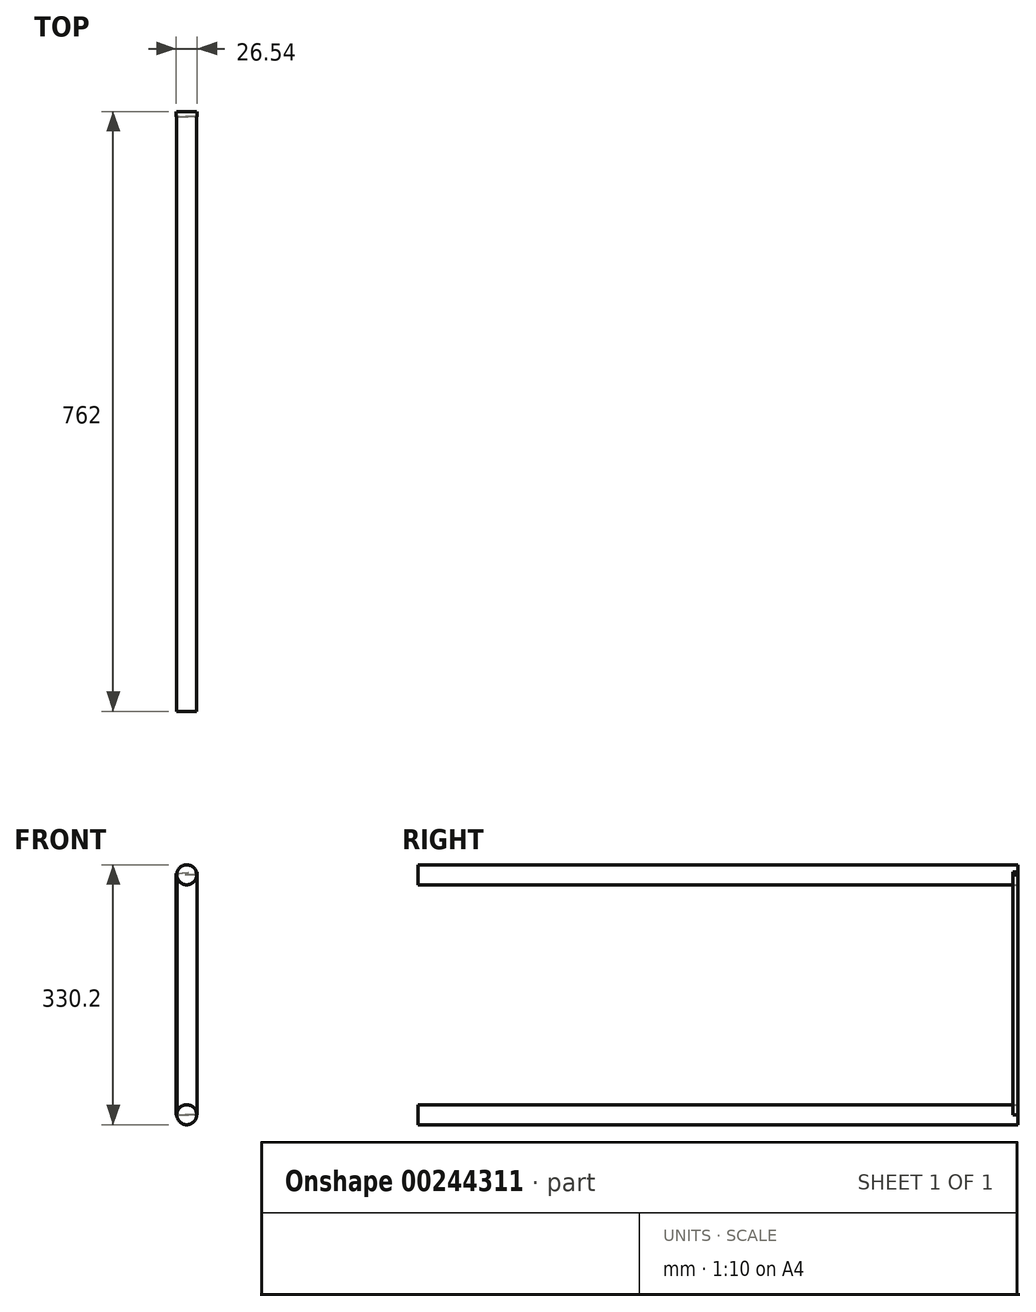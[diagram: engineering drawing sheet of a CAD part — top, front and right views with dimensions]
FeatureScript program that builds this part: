
annotation { "Feature Type Name" : "Feature", "Feature Type Description" : "" }
export const myFeature = defineFeature(function(context is Context, id is Id, definition is map)
    precondition{}
    {
        {
            var Q0;
            Q0=qCreatedBy(makeId("Front.planeOp"),FACE);
            var sketch = newSketch(context, id + "F0", { "sketchPlane" : qUnion([Q0])});
            skCircle(sketch, "E0", {"center": v(0, 0) * mm, "radius": 12.7 * mm});
            skSolve(sketch);
        }
        {
            var Q0;
            Q0=makeQuery(id+"F0.imprint","IMPRINT",FACE,{"disambiguationData":[TD([[makeQuery(id+"F0.imprint","IMPRINT",EDGE,{"derivedFrom":sQuery(id+"F0.wireOp",EDGE,"E0")}),1.0]])]});
            extrude(context, id + "F1", {"entities" : qUnion([Q0]), "depth" : 762 * mm});
        }
        {
            var Q0;
            Q0=qCreatedBy(makeId("Front.planeOp"),FACE);
            var sketch = newSketch(context, id + "F2", { "sketchPlane" : qUnion([Q0])});
            skLineSegment(sketch, "E1", {"start": v(0, 0) * mm, "end": v(0, 304.8) * mm});
            skCircle(sketch, "E2", {"center": v(0, 304.8) * mm, "radius": 12.7 * mm});
            skSolve(sketch);
        }
        {
            var Q0;
            Q0=makeQuery(id+"F2.imprint","IMPRINT",FACE,{"disambiguationData":[TD([[makeQuery(id+"F2.imprint","IMPRINT",EDGE,{"derivedFrom":sQuery(id+"F2.wireOp",EDGE,"E2")}),1.0]])]});
            extrude(context, id + "F3", {"entities" : qUnion([Q0]), "depth" : 762 * mm});
        }
        {
            var Q0;
            Q0=qCreatedBy(makeId("Front.planeOp"),FACE);
            var sketch = newSketch(context, id + "F4", { "sketchPlane" : qUnion([Q0])});
            skLineSegment(sketch, "E3", {"start": v(13.28, 304.8) * mm, "end": v(13.28, 0) * mm});
            skLineSegment(sketch, "E4", {"start": v(-12.54, 304.8) * mm, "end": v(-12.54, 0) * mm});
            skLineSegment(sketch, "E5", {"start": v(13.28, 0) * mm, "end": v(-12.54, 0) * mm});
            skLineSegment(sketch, "E6", {"start": v(13.28, 304.8) * mm, "end": v(-12.54, 304.8) * mm});
            skSolve(sketch);
        }
        {
            var Q0;
            Q0 = qSketchRegion(id + "F4", true);
            extrude(context, id + "F5", {"entities" : qUnion([Q0]), "depth" : 6.35 * mm});
        }
        {
            var Q0;
            Q0=qCreatedBy(makeId("Front.planeOp"),FACE);
            var sketch = newSketch(context, id + "F6", { "sketchPlane" : qUnion([Q0])});
            skLineSegment(sketch, "E7", {"start": v(-13.26, 306.71) * mm, "end": v(-13.26, 0) * mm});
            skLineSegment(sketch, "E8", {"start": v(13.26, 0) * mm, "end": v(13.26, 308.18) * mm});
            skLineSegment(sketch, "E9", {"start": v(-13.26, 306.71) * mm, "end": v(13.26, 308.18) * mm});
            skLineSegment(sketch, "E10", {"start": v(-13.26, 0) * mm, "end": v(13.26, 0) * mm});
            skSolve(sketch);
        }
        {
            var Q0;
            Q0 = qSketchRegion(id + "F6", true);
            extrude(context, id + "F7", {"entities" : qUnion([Q0]), "depth" : 6.35 * mm});
        }
        {
            var Q0;
            Q0=makeQuery(id+"F7.opExtrude","CAP_FACE",FACE,{"disambiguationData":[OSD([sQuery(id+"F6.wireOp",EDGE,"E7"),sQuery(id+"F6.wireOp",EDGE,"E8"),sQuery(id+"F6.wireOp",EDGE,"E9"),sQuery(id+"F6.wireOp",EDGE,"E10")])],"isStart":false});
            var sketch = newSketch(context, id + "F8", { "sketchPlane" : qUnion([Q0])});
            skLineSegment(sketch, "E11", {"start": v(-247.39, 0) * mm, "end": v(-247.39, -295.51) * mm});
            skLineSegment(sketch, "E12", {"start": v(-272.44, 0) * mm, "end": v(-272.44, -300.67) * mm});
            skLineSegment(sketch, "E13", {"start": v(-272.44, -300.67) * mm, "end": v(-247.39, -295.51) * mm});
            skLineSegment(sketch, "E14", {"start": v(-272.44, 0) * mm, "end": v(-247.39, 0) * mm});
            skSolve(sketch);
        }
        {
            var Q0;
            Q0 = qSketchRegion(id + "F8", true);
            extrude(context, id + "F9", {"entities" : qUnion([Q0]), "depth" : 6.35 * mm});
        }
        {
            var Q0;
            Q0=makeQuery(id+"F9.opExtrude","SWEPT_BODY",BODY,{"disambiguationData":[OSD([sQuery(id+"F8.wireOp",EDGE,"E11"),sQuery(id+"F8.wireOp",EDGE,"E12"),sQuery(id+"F8.wireOp",EDGE,"E13"),sQuery(id+"F8.wireOp",EDGE,"E14")])]});
            deleteBodies(context, id + "F10", {"entities" : qUnion([Q0])});
        }
    });
